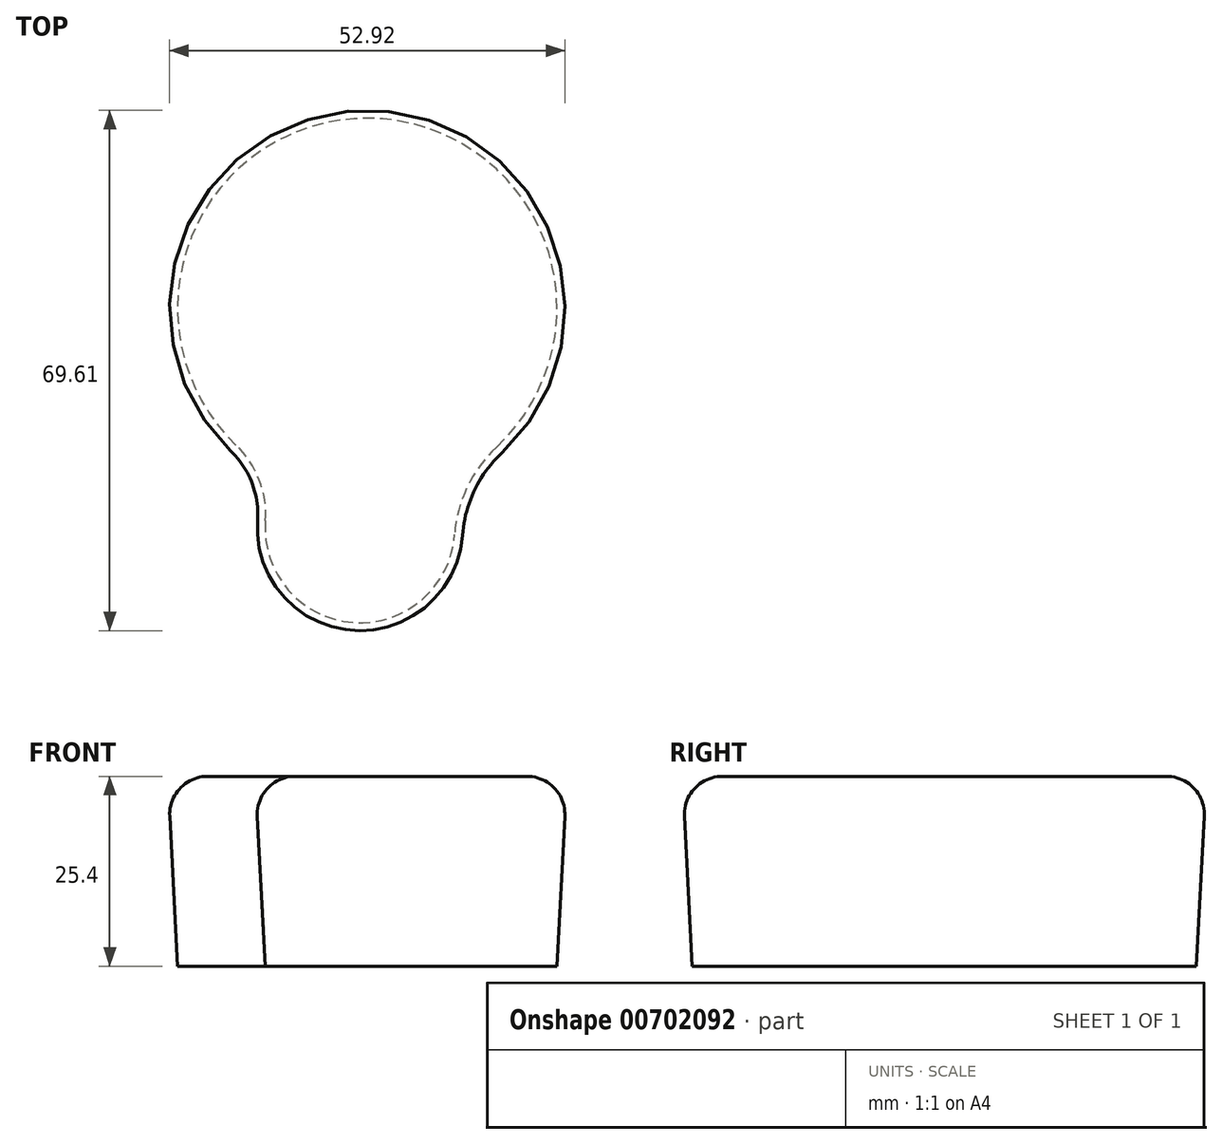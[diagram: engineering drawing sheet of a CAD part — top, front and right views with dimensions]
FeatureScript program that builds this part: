
annotation { "Feature Type Name" : "Feature", "Feature Type Description" : "" }
export const myFeature = defineFeature(function(context is Context, id is Id, definition is map)
    precondition{}
    {
        {
            var Q0;
            Q0=qCreatedBy(makeId("Top.planeOp"),FACE);
            var sketch = newSketch(context, id + "F0", { "sketchPlane" : qUnion([Q0])});
            skArc(sketch, "E0", {"start": v(-51.68, -23.33) * mm, "mid": v(-39.94, -36.92) * mm, "end": v(-26.35, -25.17) * mm});
            skArc(sketch, "E1", {"start": v(-20.73, -13.45) * mm, "mid": v(-37.88, 30.54) * mm, "end": v(-55.58, -13.23) * mm});
            skPoint(sketch, "E2.visualSharp", {"position": v(-27.89, -18.14) * mm});
            skArc(sketch, "E2.filletArc", {"start": v(-20.73, -13.45) * mm, "mid": v(-24.65, -18.78) * mm, "end": v(-26.35, -25.17) * mm});
            skPoint(sketch, "E3.visualSharp", {"position": v(-49.72, -17.41) * mm});
            skArc(sketch, "E3.filletArc", {"start": v(-51.68, -23.33) * mm, "mid": v(-52.5, -17.85) * mm, "end": v(-55.58, -13.23) * mm});
            skSolve(sketch);
        }
        {
            var Q0;
            Q0=makeQuery(id+"F0.imprint","IMPRINT",FACE,{"disambiguationData":[TD([[makeQuery(id+"F0.imprint","IMPRINT",EDGE,{"derivedFrom":sQuery(id+"F0.wireOp",EDGE,"E0")}),1.0]])]});
            extrude(context, id + "F1", {"entities" : qUnion([Q0]), "depth" : 25.4 * mm, "offsetDistance" : 25.4 * mm, "hasDraft" : true, "draftAngle" : 3 * degree});
        }
        {
            var Q0;
            Q0=makeQuery(id+"F1.opExtrude","CAP_EDGE",EDGE,{"disambiguationData":[OSD([sQuery(id+"F0.wireOp",EDGE,"E1")])],"isStart":false});
            fillet(context, id + "F2", {"entities" : qUnion([Q0]), "radius" : 5.08 * mm, "tangentPropagation" : true, "allowEdgeOverflow" : false});
        }
    });
